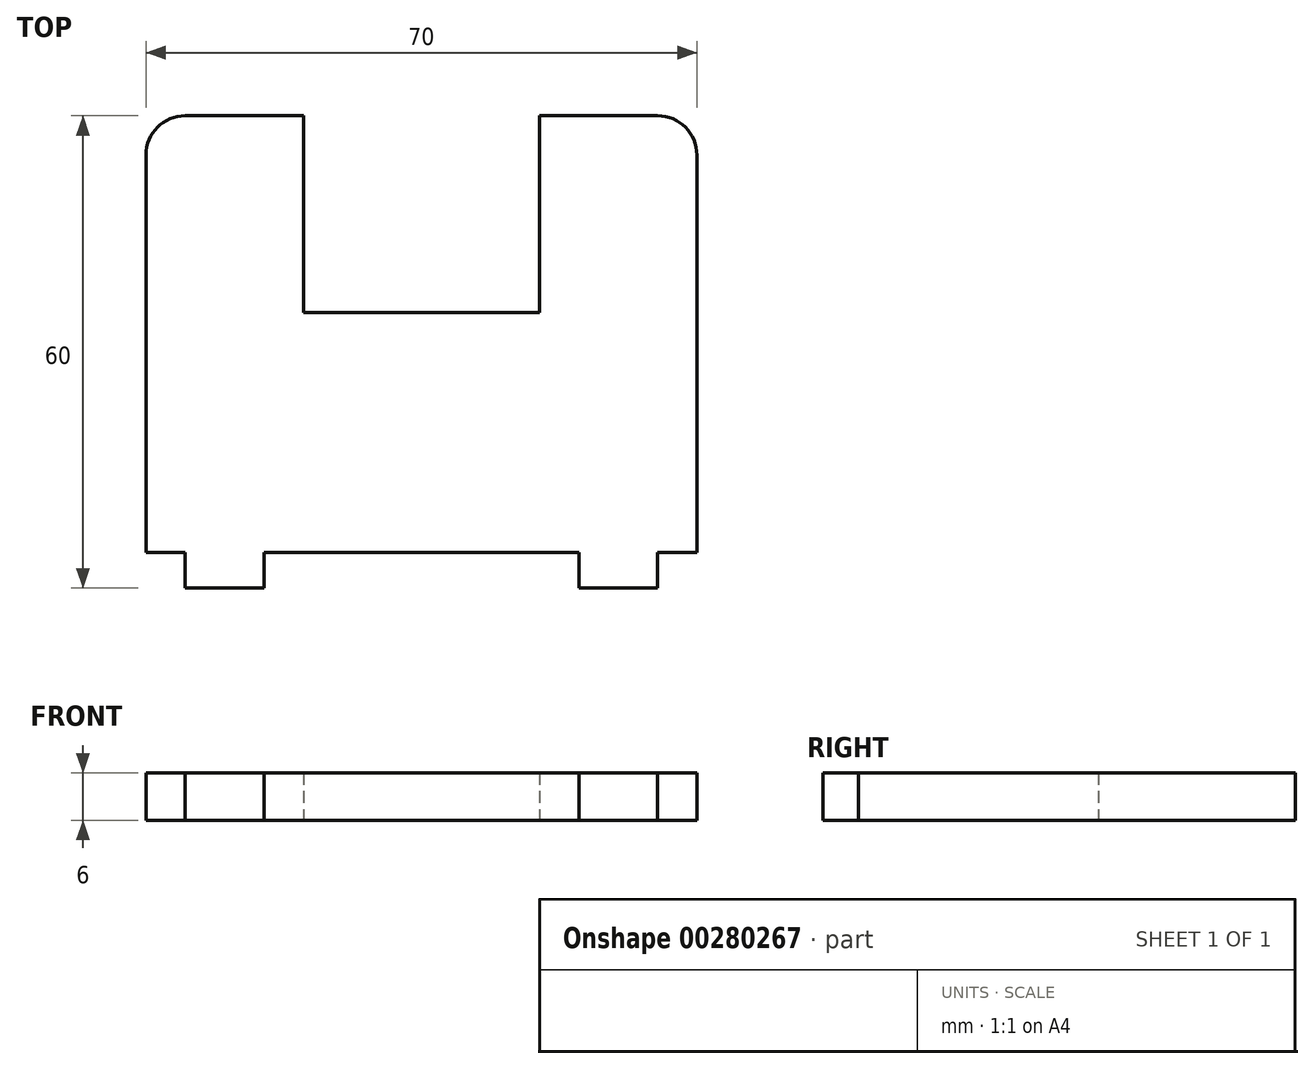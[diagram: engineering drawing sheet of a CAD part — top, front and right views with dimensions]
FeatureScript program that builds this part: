
annotation { "Feature Type Name" : "Feature", "Feature Type Description" : "" }
export const myFeature = defineFeature(function(context is Context, id is Id, definition is map)
    precondition{}
    {
        {
            var Q0;
            Q0=qCreatedBy(makeId("Top.planeOp"),FACE);
            var sketch = newSketch(context, id + "F0", { "sketchPlane" : qUnion([Q0])});
            skLineSegment(sketch, "E0", {"start": v(-35, -30.5) * mm, "end": v(-30, -30.5) * mm});
            skLineSegment(sketch, "E1", {"start": v(-30, -30.5) * mm, "end": v(-30, -35) * mm});
            skLineSegment(sketch, "E2", {"start": v(-30, -35) * mm, "end": v(-20, -35) * mm});
            skLineSegment(sketch, "E3", {"start": v(-20, -35) * mm, "end": v(-20, -30.5) * mm});
            skLineSegment(sketch, "E4", {"start": v(-20, -30.5) * mm, "end": v(20, -30.5) * mm});
            skLineSegment(sketch, "E5", {"start": v(20, -30.5) * mm, "end": v(20, -35) * mm});
            skLineSegment(sketch, "E6", {"start": v(20, -35) * mm, "end": v(30, -35) * mm});
            skLineSegment(sketch, "E7", {"start": v(30, -35) * mm, "end": v(30, -30.5) * mm});
            skLineSegment(sketch, "E8", {"start": v(30, -30.5) * mm, "end": v(35, -30.5) * mm});
            skLineSegment(sketch, "E9", {"start": v(35, -30.5) * mm, "end": v(35, 20) * mm});
            skLineSegment(sketch, "E10", {"start": v(30, 25) * mm, "end": v(15, 25) * mm});
            skLineSegment(sketch, "E11", {"start": v(15, 25) * mm, "end": v(15, 0) * mm});
            skLineSegment(sketch, "E12", {"start": v(15, 0) * mm, "end": v(-15, 0) * mm});
            skLineSegment(sketch, "E13", {"start": v(-15, 0) * mm, "end": v(-15, 25) * mm});
            skLineSegment(sketch, "E14", {"start": v(-15, 25) * mm, "end": v(-30, 25) * mm});
            skLineSegment(sketch, "E15", {"start": v(-35, 20) * mm, "end": v(-35, -30.5) * mm});
            skPoint(sketch, "E16", {"position": v(0, 0) * mm});
            skPoint(sketch, "E17", {"position": v(-25, -35) * mm});
            skPoint(sketch, "E18", {"position": v(25, -35) * mm});
            skPoint(sketch, "E19.visualSharp", {"position": v(-35, 25) * mm});
            skArc(sketch, "E19.filletArc", {"start": v(-30, 25) * mm, "mid": v(-33.54, 23.54) * mm, "end": v(-35, 20) * mm});
            skPoint(sketch, "E20.visualSharp", {"position": v(35, 25) * mm});
            skArc(sketch, "E20.filletArc", {"start": v(35, 20) * mm, "mid": v(33.54, 23.54) * mm, "end": v(30, 25) * mm});
            skSolve(sketch);
        }
        {
            var Q0;
            Q0=makeQuery(id+"F0.imprint","IMPRINT",FACE,{"disambiguationData":[TD([[makeQuery(id+"F0.imprint","IMPRINT",EDGE,{"derivedFrom":sQuery(id+"F0.wireOp",EDGE,"E0")}),1.0]])]});
            extrude(context, id + "F1", {"entities" : qUnion([Q0]), "depth" : 6 * mm});
        }
    });
